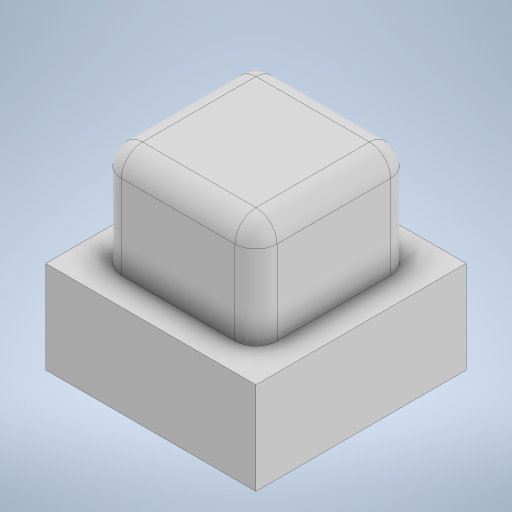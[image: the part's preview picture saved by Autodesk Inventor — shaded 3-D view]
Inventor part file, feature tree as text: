
AUTODESK INVENTOR PART (.ipt)
format: ipt  version: 2024 (Build 280153000, 153)  size: 248,320 bytes
history: native  units: mm
features: extrude x3, sketch x3, fillet x2
ambient origin geometry x8: Origin, YZ Plane, XZ Plane, XY Plane, X Axis, Y Axis, Z Axis, Center Point
bodies: Body1 (feature_tree)
feature tree (8):
  extrude  "Extrusion5"  Depth=5.0mm
  extrude  "Extrusion6"  Depth=5.0mm
  extrude  "Extrusion7"  Depth=2.195mm TaperAngle=0.0deg
  fillet  "Congé2"  Radius=3.7mm
  fillet  "Congé3"  Radius=1.195mm
  sketch  "Esquisse6"
  sketch  "Esquisse7"
  sketch  "Esquisse8"
